# Revit family: Shower_Valve-DXV-D35101SS0.191
name_source: partatom
category: Plumbing Fixtures
units: mm (PartAtom-declared; Revit-internal decimal feet)

## family parameters
Always vertical = No
Cut with Voids When Loaded = No
OmniClass Number = 23.45.05.14.17
OmniClass Title = Showers
Part Type = Normal
Room Calculation Point = No
Round Connector Dimension = Use Diameter
Shared = Yes
Work Plane-Based = No

## types (1)
- D35101SS0.191
    CW Connection = Yes
    CWFU = 3
    Connection Diameter = 1/2"
    Connection Outlet Description 1 = 1/2" Temperred Outlet Connection 1
    Connection Outlet Description 2 = 1/2" Temperred Outlet Connection 2
    Description = PBV10 ROUGH IN VALVE
    Finish = Metal-DXV-Brass
    HW Connection = Yes
    HWFU = 3
    Height = 3 5/8"
    IAPMO Compliance = Meets or Exceeds ASSE 1016 / ASME A112.18.1016 /CSA B125.16ASME A112.18.1 / CSA B125.1
    Length = 4 7/8"
    Manufacturer = DXV
    Material = Metal-DXV-Brass
    Model = D35101SS0.191
    Product Documentation Link = https://dxv01.blob.core.windows.net
    Product Page URL = https://www.dxv.com
    Tempered Water Connection = Yes
    URL = https://www.dxv.com
    Vent Connection = No
    WFU = 4
    Waste Connection = No
    Width = 2 3/4"
    Width Constraint = 2 3/4"

## geometry (parser evidence)
native form markers: Sweep x2
no freeform markers — native parametric forms only
